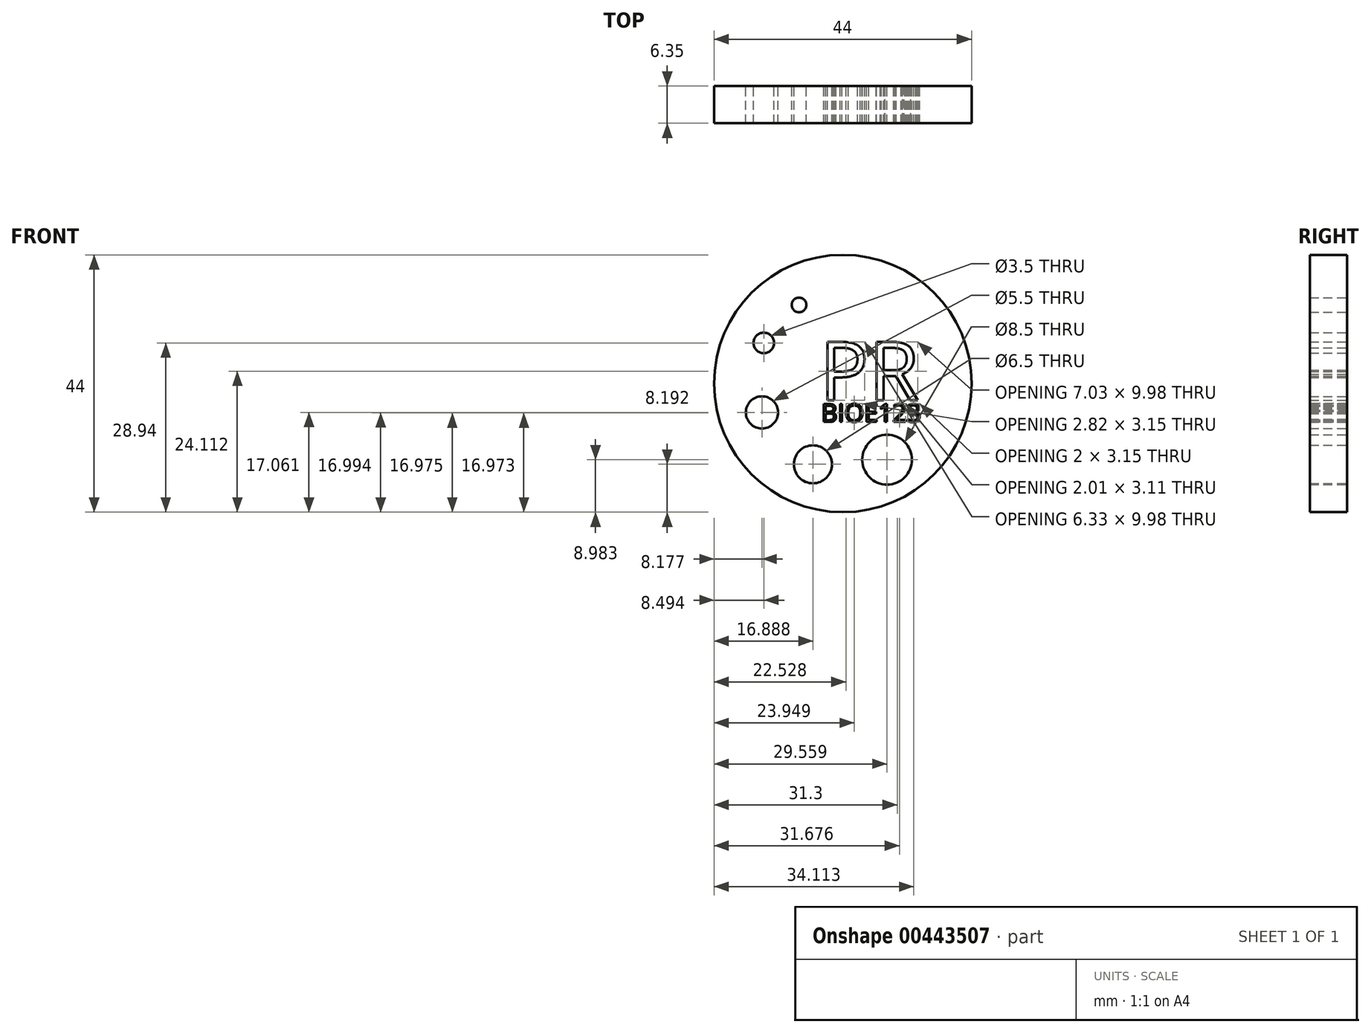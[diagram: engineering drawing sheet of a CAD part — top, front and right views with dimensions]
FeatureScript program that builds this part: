
annotation { "Feature Type Name" : "Feature", "Feature Type Description" : "" }
export const myFeature = defineFeature(function(context is Context, id is Id, definition is map)
    precondition{}
    {
        {
            var Q0;
            Q0=qCreatedBy(makeId("Front.planeOp"),FACE);
            var sketch = newSketch(context, id + "F0", { "sketchPlane" : qUnion([Q0])});
            skCircle(sketch, "E0", {"center": v(0, 0) * mm, "radius": 22 * mm});
            skCircle(sketch, "E1", {"center": v(-7.49, 13.43) * mm, "radius": 1.25 * mm});
            skCircle(sketch, "E2", {"center": v(-13.5, 6.94) * mm, "radius": 1.75 * mm});
            skCircle(sketch, "E3", {"center": v(-13.82, -4.94) * mm, "radius": 2.75 * mm});
            skCircle(sketch, "E4", {"center": v(7.56, -13.02) * mm, "radius": 4.25 * mm});
            skCircle(sketch, "E5", {"center": v(-5.11, -13.8) * mm, "radius": 3.25 * mm});
            skText(sketch, "E6", { "text": "PR", "fontName": "OpenSans-Regular.ttf"});
            skText(sketch, "E7", { "text": "BIOE123", "fontName": "OpenSans-Regular.ttf"});
            const initialGuessF0  = {"E6": [-0.00401, -0.00288, 1, 0, 0.01007], "E7": [-0.0037, -0.00656, 1, 0, 0.00309]};
            skSetInitialGuess(sketch, initialGuessF0);
            skSolve(sketch);
        }
        {
            var Q0;
            Q0=makeQuery(id+"F0.imprint","IMPRINT",FACE,{"disambiguationData":[TD([[makeQuery(id+"F0.imprint","IMPRINT",EDGE,{"derivedFrom":sQuery(id+"F0.wireOp",EDGE,"E7.sketch_text.stroke-37")}),1.0]])]});
            var Q1;
            Q1=makeQuery(id+"F0.imprint","IMPRINT",FACE,{"disambiguationData":[TD([[makeQuery(id+"F0.imprint","IMPRINT",EDGE,{"derivedFrom":sQuery(id+"F0.wireOp",EDGE,"E7.sketch_text.stroke-11")}),1.0]])]});
            var Q2;
            Q2=makeQuery(id+"F0.imprint","IMPRINT",FACE,{"disambiguationData":[TD([[makeQuery(id+"F0.imprint","IMPRINT",EDGE,{"derivedFrom":sQuery(id+"F0.wireOp",EDGE,"E7.sketch_text.stroke-18")}),1.0]])]});
            var Q3;
            Q3=makeQuery(id+"F0.imprint","IMPRINT",FACE,{"disambiguationData":[TD([[makeQuery(id+"F0.imprint","IMPRINT",EDGE,{"derivedFrom":sQuery(id+"F0.wireOp",EDGE,"E6.sketch_text.stroke-8")}),1.0]])]});
            var Q4;
            Q4=makeQuery(id+"F0.imprint","IMPRINT",FACE,{"disambiguationData":[TD([[makeQuery(id+"F0.imprint","IMPRINT",EDGE,{"derivedFrom":sQuery(id+"F0.wireOp",EDGE,"E6.sketch_text.stroke-26")}),1.0]])]});
            var Q5;
            Q5=makeQuery(id+"F0.imprint","IMPRINT",FACE,{"disambiguationData":[TD([[makeQuery(id+"F0.imprint","IMPRINT",EDGE,{"derivedFrom":sQuery(id+"F0.wireOp",EDGE,"E0")}),1.0]])]});
            extrude(context, id + "F1", {"entities" : qUnion([Q0, Q1, Q2, Q3, Q4, Q5]), "depth" : 6.35 * mm});
        }
    });
